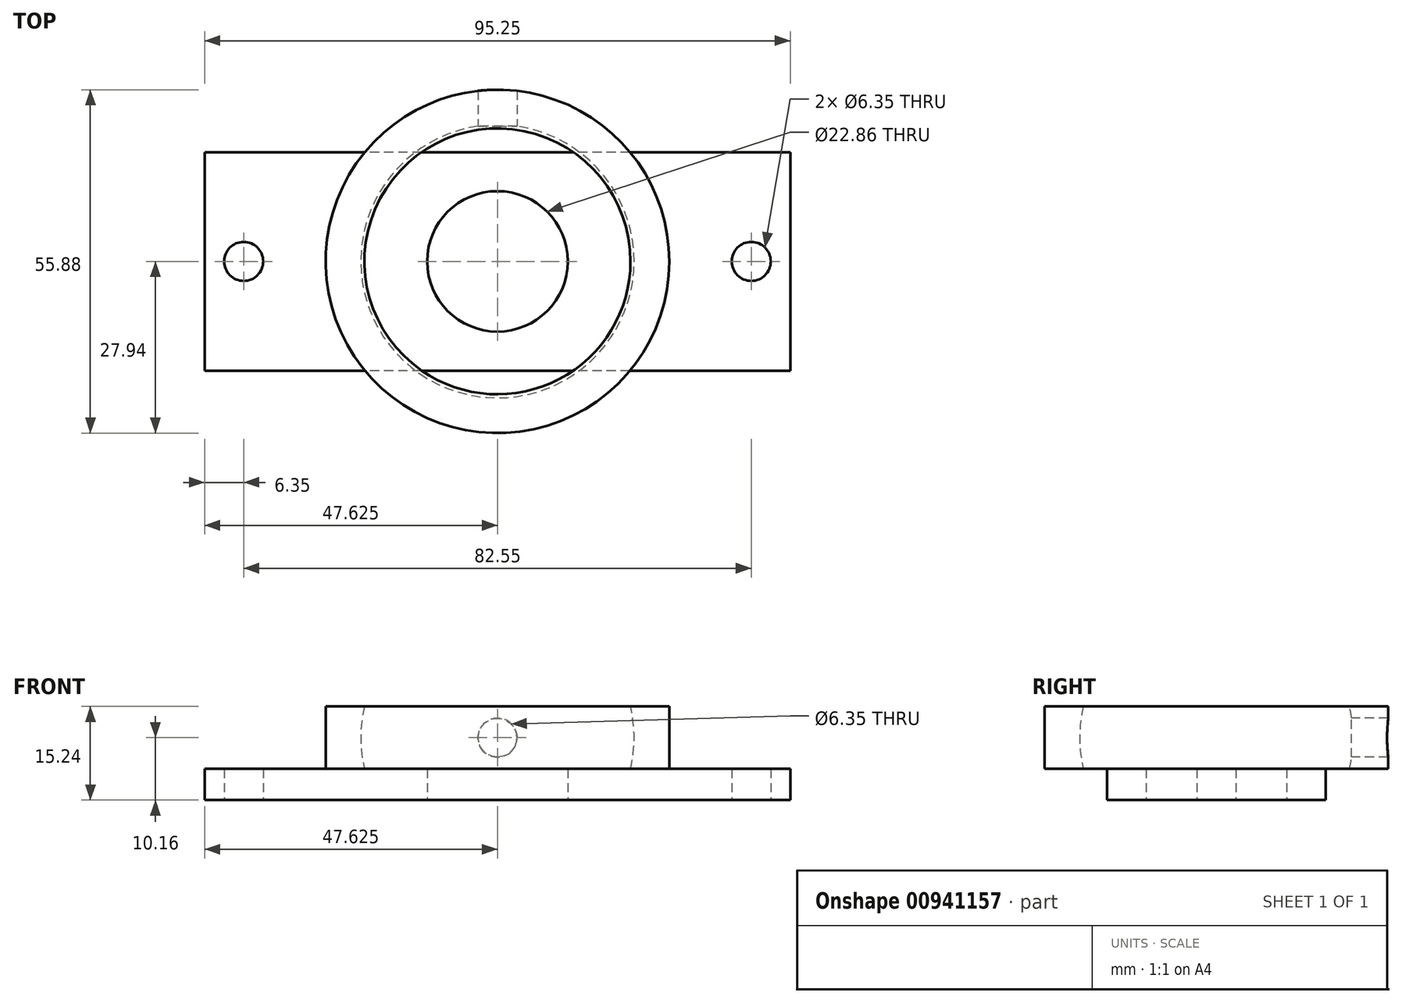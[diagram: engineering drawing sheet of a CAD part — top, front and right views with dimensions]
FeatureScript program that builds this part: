
annotation { "Feature Type Name" : "Feature", "Feature Type Description" : "" }
export const myFeature = defineFeature(function(context is Context, id is Id, definition is map)
    precondition{}
    {
        {
            var Q0;
            Q0=qCreatedBy(makeId("Top.planeOp"),FACE);
            var sketch = newSketch(context, id + "F0", { "sketchPlane" : qUnion([Q0])});
            skCircle(sketch, "E0", {"center": v(0, 0) * mm, "radius": 3.18 * mm});
            skLineSegment(sketch, "E1.bottom", {"start": v(6.35, 17.78) * mm, "end": v(-88.9, 17.78) * mm});
            skLineSegment(sketch, "E1.top", {"start": v(6.35, -17.78) * mm, "end": v(-88.9, -17.78) * mm});
            skLineSegment(sketch, "E1.left", {"start": v(6.35, 17.78) * mm, "end": v(6.35, -17.78) * mm});
            skLineSegment(sketch, "E1.right", {"start": v(-88.9, 17.78) * mm, "end": v(-88.9, -17.78) * mm});
            skCircle(sketch, "E2", {"center": v(-82.55, 0) * mm, "radius": 3.18 * mm});
            skCircle(sketch, "E3", {"center": v(-41.28, 0) * mm, "radius": 11.43 * mm});
            skSolve(sketch);
        }
        {
            var Q0;
            Q0=makeQuery(id+"F0.imprint","IMPRINT",FACE,{"disambiguationData":[TD([[makeQuery(id+"F0.imprint","IMPRINT",EDGE,{"derivedFrom":sQuery(id+"F0.wireOp",EDGE,"E0")}),-1.0]])]});
            extrude(context, id + "F1", {"entities" : qUnion([Q0]), "depth" : 5.08 * mm, "offsetDistance" : 25.4 * mm});
        }
        {
            var Q0;
            Q0=makeQuery(id+"F1.opExtrude","CAP_FACE",FACE,{"disambiguationData":[OSD([sQuery(id+"F0.wireOp",EDGE,"E0"),sQuery(id+"F0.wireOp",EDGE,"E1.bottom"),sQuery(id+"F0.wireOp",EDGE,"E1.top"),sQuery(id+"F0.wireOp",EDGE,"E1.left"),sQuery(id+"F0.wireOp",EDGE,"E1.right"),sQuery(id+"F0.wireOp",EDGE,"E2"),sQuery(id+"F0.wireOp",EDGE,"E3")])],"isStart":false});
            var sketch = newSketch(context, id + "F2", { "sketchPlane" : qUnion([Q0])});
            skCircle(sketch, "E4", {"center": v(-41.28, 0) * mm, "radius": 27.94 * mm});
            skSolve(sketch);
        }
        {
            var Q0;
            Q0=makeQuery(id+"F2.imprint","IMPRINT",FACE,{"disambiguationData":[TD([[makeQuery(id+"F2.imprint","IMPRINT",EDGE,{"derivedFrom":makeQuery(id+"F1.opExtrude","CAP_EDGE",EDGE,{"disambiguationData":[OSD([sQuery(id+"F0.wireOp",EDGE,"E3")])],"isStart":false})}),-1.0]])]});
            var Q1;
            {var subQ0=sQuery(id+"F2.wireOp",EDGE,"E4");var subQ1=makeQuery(id+"F1.opExtrude","CAP_EDGE",EDGE,{"disambiguationData":[OSD([sQuery(id+"F0.wireOp",EDGE,"E1.bottom")])],"isStart":false});var subQ2=makeQuery(id+"F2.imprint","INTERSECT",VERTEX,{"disambiguationData":[OD(0.0)],"derivedFrom":[subQ1,subQ0]});Q1=makeQuery(id+"F2.imprint","IMPRINT",FACE,{"disambiguationData":[TD([[makeQuery(id+"F2.imprint","IMPRINT",EDGE,{"disambiguationData":[TD([[subQ2,1.0]])],"derivedFrom":subQ0}),1.0]])]});}
            var Q2;
            {var subQ0=sQuery(id+"F2.wireOp",EDGE,"E4");var subQ1=makeQuery(id+"F1.opExtrude","CAP_EDGE",EDGE,{"disambiguationData":[OSD([sQuery(id+"F0.wireOp",EDGE,"E1.top")])],"isStart":false});var subQ2=makeQuery(id+"F2.imprint","INTERSECT",VERTEX,{"disambiguationData":[OD(0.0)],"derivedFrom":[subQ1,subQ0]});Q2=makeQuery(id+"F2.imprint","IMPRINT",FACE,{"disambiguationData":[TD([[makeQuery(id+"F2.imprint","IMPRINT",EDGE,{"disambiguationData":[TD([[subQ2,-1.0]])],"derivedFrom":subQ0}),1.0]])]});}
            extrude(context, id + "F3", {"entities" : qUnion([Q0, Q1, Q2]), "operationType" : NewBodyOperationType.ADD, "depth" : 10.16 * mm, "offsetDistance" : 25.4 * mm});
        }
        {
            var Q0;
            Q0=qCreatedBy(makeId("Right.planeOp"),FACE);
            cPlane(context, id + "F4", {"entities" : qUnion([Q0]), "cplaneType" : CPlaneType.OFFSET, "offset" : 41.27 * mm, "oppositeDirection" : true, "width" : 152.4 * mm, "height" : 152.4 * mm});
        }
        {
            var Q0;
            Q0=qCreatedBy(id+"F4.planeOp",FACE);
            var sketch = newSketch(context, id + "F5", { "sketchPlane" : qUnion([Q0])});
            skPoint(sketch, "E5", {"position": v(0, 10.16) * mm});
            skLineSegment(sketch, "E6", {"start": v(0, 10.16) * mm, "end": v(-21.64, 5.08) * mm});
            skLineSegment(sketch, "E7", {"start": v(0, 10.16) * mm, "end": v(21.64, 5.08) * mm});
            skLineSegment(sketch, "E8", {"start": v(0, 10.16) * mm, "end": v(0, 32.39) * mm});
            skArc(sketch, "E9", {"start": v(21.64, 5.08) * mm, "mid": v(0, 32.39) * mm, "end": v(-21.64, 5.08) * mm});
            skLineSegment(sketch, "E10", {"start": v(-21.64, 5.08) * mm, "end": v(0, 5.08) * mm});
            skLineSegment(sketch, "E11", {"start": v(0, 5.08) * mm, "end": v(0, 10.16) * mm});
            skSolve(sketch);
        }
        {
            var Q0;
            Q0=makeQuery(id+"F5.imprint","IMPRINT",FACE,{"disambiguationData":[TD([[makeQuery(id+"F5.imprint","IMPRINT",EDGE,{"derivedFrom":sQuery(id+"F5.wireOp",EDGE,"E6")}),1.0]])]});
            var Q1;
            {var subQ0=sQuery(id+"F5.wireOp",EDGE,"E6");Q1=makeQuery(id+"F5.imprint","IMPRINT",FACE,{"disambiguationData":[TD([[makeQuery(id+"F5.imprint","IMPRINT",EDGE,{"derivedFrom":subQ0}),-1.0]])]});}
            var Q2;
            Q2=sQuery(id+"F5.wireOp",EDGE,"E8");
            revolve(context, id + "F6", {"operationType" : NewBodyOperationType.REMOVE, "surfaceOperationType" : NewSurfaceOperationType.NEW, "entities" : qUnion([Q0, Q1]), "axis" : qUnion([Q2]), "revolveType" : RevolveType.FULL, "oppositeDirection" : true});
        }
        {
            var Q0;
            Q0=qCreatedBy(makeId("Front.planeOp"),FACE);
            var sketch = newSketch(context, id + "F7", { "sketchPlane" : qUnion([Q0])});
            skPoint(sketch, "E12", {"position": v(-41.28, 10.16) * mm});
            skSolve(sketch);
        }
        {
            var Q0;
            Q0=sQuery(id+"F7.wireOp",VERTEX,"E12");
            var Q1;
            Q1=makeQuery(id+"F1.opExtrude","SWEPT_BODY",BODY,{"disambiguationData":[OSD([sQuery(id+"F0.wireOp",EDGE,"E0"),sQuery(id+"F0.wireOp",EDGE,"E1.bottom"),sQuery(id+"F0.wireOp",EDGE,"E1.top"),sQuery(id+"F0.wireOp",EDGE,"E1.left"),sQuery(id+"F0.wireOp",EDGE,"E1.right"),sQuery(id+"F0.wireOp",EDGE,"E2"),sQuery(id+"F0.wireOp",EDGE,"E3")])]});
            hole(context, id + "F8", {"style" : HoleStyle.SIMPLE, "endStyle" : HoleEndStyle.THROUGH, "holeDiameter" : 6.35 * mm, "majorDiameter" : 6.35 * mm, "isTappedThrough" : true, "tappedDepth" : 12.7 * mm, "tapClearance" : 3, "locations" : qUnion([Q0]), "scope" : qUnion([Q1])});
        }
    });
